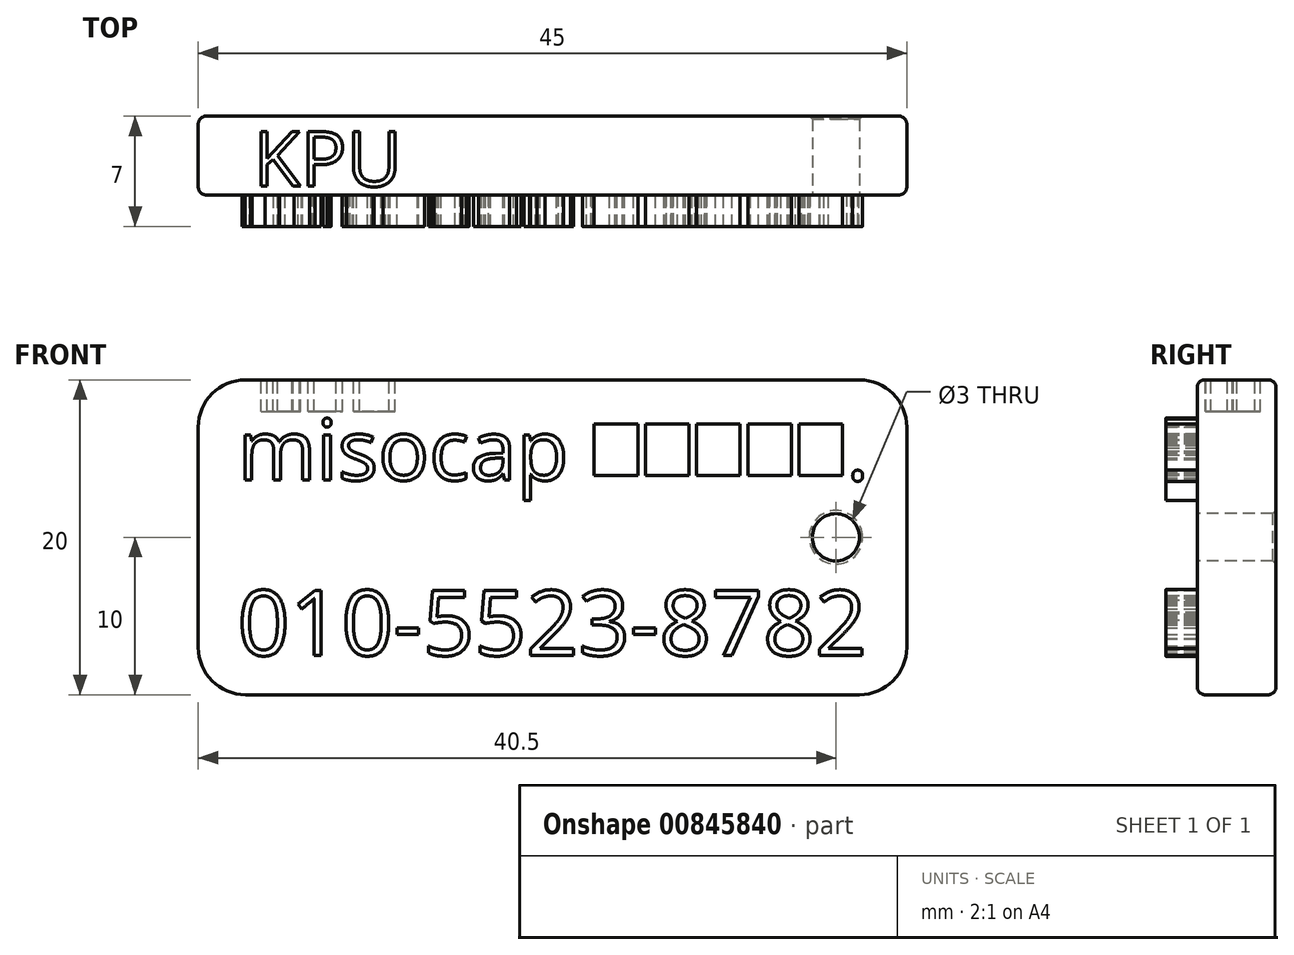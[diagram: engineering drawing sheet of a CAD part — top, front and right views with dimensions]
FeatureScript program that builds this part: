
annotation { "Feature Type Name" : "Feature", "Feature Type Description" : "" }
export const myFeature = defineFeature(function(context is Context, id is Id, definition is map)
    precondition{}
    {
        {
            var Q0;
            Q0=qCreatedBy(makeId("Front.planeOp"),FACE);
            var sketch = newSketch(context, id + "F0", { "sketchPlane" : qUnion([Q0])});
            skLineSegment(sketch, "E0.bottom", {"start": v(22.5, 10) * mm, "end": v(-22.5, 10) * mm});
            skLineSegment(sketch, "E0.top", {"start": v(22.5, -10) * mm, "end": v(-22.5, -10) * mm});
            skLineSegment(sketch, "E0.left", {"start": v(22.5, 10) * mm, "end": v(22.5, -10) * mm});
            skLineSegment(sketch, "E0.right", {"start": v(-22.5, 10) * mm, "end": v(-22.5, -10) * mm});
            skPoint(sketch, "E0.middle", {"position": v(0, 0) * mm});
            skSolve(sketch);
        }
        {
            var Q0;
            Q0 = qSketchRegion(id + "F0", true);
            extrude(context, id + "F1", {"entities" : qUnion([Q0]), "depth" : 5 * mm, "offsetDistance" : 25 * mm});
        }
        {
            var Q0;
            Q0=makeQuery(id+"F1.opExtrude","CAP_FACE",FACE,{"disambiguationData":[OSD([sQuery(id+"F0.wireOp",EDGE,"E0.bottom"),sQuery(id+"F0.wireOp",EDGE,"E0.top"),sQuery(id+"F0.wireOp",EDGE,"E0.left"),sQuery(id+"F0.wireOp",EDGE,"E0.right")])],"isStart":false});
            var sketch = newSketch(context, id + "F2", { "sketchPlane" : qUnion([Q0])});
            skText(sketch, "E1", { "text": "misocap 반갑습니다.", "fontName": "OpenSans-Regular.ttf"});
            const initialGuessF2  = {"E1": [-0.02, 0.00363, 1, 0, 0.00387]};
            skSetInitialGuess(sketch, initialGuessF2);
            skSolve(sketch);
        }
        {
            var Q0;
            Q0 = qSketchRegion(id + "F2", true);
            extrude(context, id + "F3", {"entities" : qUnion([Q0]), "operationType" : NewBodyOperationType.ADD, "depth" : 2 * mm, "offsetDistance" : 25 * mm});
        }
        {
            var Q0;
            {var subQ0=sQuery(id+"F0.wireOp",EDGE,"E0.top");var subQ1=sQuery(id+"F0.wireOp",EDGE,"E0.right");var subQ2=sQuery(id+"F0.wireOp",EDGE,"E0.bottom");var subQ3=sQuery(id+"F0.wireOp",EDGE,"E0.left");Q0=makeQuery(id+"F3.boolean.opBoolean","SPLIT",FACE,{"disambiguationData":[TD([makeQuery(id+"F1.opExtrude","SWEPT_FACE",FACE,{"disambiguationData":[OSD([subQ2])]})])],"derivedFrom":makeQuery(id+"F1.opExtrude","CAP_FACE",FACE,{"disambiguationData":[OSD([subQ2,subQ0,subQ3,subQ1])],"isStart":false})});}
            var sketch = newSketch(context, id + "F4", { "sketchPlane" : qUnion([Q0])});
            skText(sketch, "E2", { "text": "010-5523-8782", "fontName": "OpenSans-Regular.ttf"});
            const initialGuessF4  = {"E2": [-0.02, -0.0075, 1, 0, 0.00415]};
            skSetInitialGuess(sketch, initialGuessF4);
            skSolve(sketch);
        }
        {
            var Q0;
            Q0 = qSketchRegion(id + "F4", true);
            extrude(context, id + "F5", {"entities" : qUnion([Q0]), "operationType" : NewBodyOperationType.ADD, "depth" : 2 * mm, "offsetDistance" : 25 * mm});
        }
        {
            var Q0;
            Q0=makeQuery(id+"F1.opExtrude","SWEPT_EDGE",EDGE,{"disambiguationData":[OSD([sQuery(id+"F0.wireOp",EDGE,"E0.bottom"),sQuery(id+"F0.wireOp",EDGE,"E0.right")])]});
            var Q1;
            Q1=makeQuery(id+"F1.opExtrude","SWEPT_EDGE",EDGE,{"disambiguationData":[OSD([sQuery(id+"F0.wireOp",EDGE,"E0.top"),sQuery(id+"F0.wireOp",EDGE,"E0.right")])]});
            var Q2;
            Q2=makeQuery(id+"F1.opExtrude","SWEPT_EDGE",EDGE,{"disambiguationData":[OSD([sQuery(id+"F0.wireOp",EDGE,"E0.top"),sQuery(id+"F0.wireOp",EDGE,"E0.left")])]});
            var Q3;
            Q3=makeQuery(id+"F1.opExtrude","SWEPT_EDGE",EDGE,{"disambiguationData":[OSD([sQuery(id+"F0.wireOp",EDGE,"E0.bottom"),sQuery(id+"F0.wireOp",EDGE,"E0.left")])]});
            fillet(context, id + "F6", {"entities" : qUnion([Q0, Q1, Q2, Q3]), "radius" : 3 * mm, "tangentPropagation" : true, "allowEdgeOverflow" : false});
        }
        {
            var Q0;
            Q0=makeQuery(id+"F1.opExtrude","SWEPT_FACE",FACE,{"disambiguationData":[OSD([sQuery(id+"F0.wireOp",EDGE,"E0.bottom")])]});
            var sketch = newSketch(context, id + "F7", { "sketchPlane" : qUnion([Q0])});
            skText(sketch, "E3", { "text": "KPU", "fontName": "OpenSans-Regular.ttf"});
            const initialGuessF7  = {"E3": [-0.019, -0.00445, 1, 0, 0.0035]};
            skSetInitialGuess(sketch, initialGuessF7);
            skSolve(sketch);
        }
        {
            var Q0;
            Q0 = qSketchRegion(id + "F7", true);
            extrude(context, id + "F8", {"entities" : qUnion([Q0]), "operationType" : NewBodyOperationType.REMOVE, "oppositeDirection" : true, "depth" : 2 * mm, "offsetDistance" : 25 * mm});
        }
        {
            var Q0;
            Q0=makeQuery(id+"F4.imprint","IMPRINT",FACE,{"disambiguationData":[TD([[makeQuery(id+"F4.imprint","IMPRINT",EDGE,{"derivedFrom":sQuery(id+"F4.wireOp",EDGE,"E2.sketch_text.stroke-0")}),1.0]])]});
            var sketch = newSketch(context, id + "F9", { "sketchPlane" : qUnion([Q0])});
            skCircle(sketch, "E4", {"center": v(18, 0) * mm, "radius": 1.5 * mm});
            skSolve(sketch);
        }
        {
            var Q0;
            Q0 = qSketchRegion(id + "F9", true);
            extrude(context, id + "F10", {"entities" : qUnion([Q0]), "operationType" : NewBodyOperationType.REMOVE, "oppositeDirection" : true, "depth" : 25 * mm, "offsetDistance" : 25 * mm});
        }
        {
            var Q0;
            Q0=makeQuery(id+"F10.boolean.opBoolean","COPY",EDGE,{"derivedFrom":makeQuery(id+"F10.opExtrude","CAP_EDGE",EDGE,{"disambiguationData":[OSD([sQuery(id+"F9.wireOp",EDGE,"E4")])],"isStart":true})});
            var Q1;
            Q1=makeQuery(id+"F10.boolean.opBoolean","INTERSECT",EDGE,{"derivedFrom":[makeQuery(id+"F1.opExtrude","CAP_FACE",FACE,{"disambiguationData":[OSD([sQuery(id+"F0.wireOp",EDGE,"E0.bottom"),sQuery(id+"F0.wireOp",EDGE,"E0.top"),sQuery(id+"F0.wireOp",EDGE,"E0.left"),sQuery(id+"F0.wireOp",EDGE,"E0.right")])],"isStart":true}),makeQuery(id+"F10.opExtrude","SWEPT_FACE",FACE,{"disambiguationData":[OSD([sQuery(id+"F9.wireOp",EDGE,"E4")])]})]});
            chamfer(context, id + "F11", {"entities" : qUnion([Q0, Q1]), "width" : 0.2 * mm, "tangentPropagation" : true});
        }
        {
            var Q0;
            Q0=makeQuery(id+"F1.opExtrude","CAP_EDGE",EDGE,{"disambiguationData":[OSD([sQuery(id+"F0.wireOp",EDGE,"E0.bottom")])],"isStart":false});
            var Q1;
            Q1=makeQuery(id+"F1.opExtrude","CAP_EDGE",EDGE,{"disambiguationData":[OSD([sQuery(id+"F0.wireOp",EDGE,"E0.bottom")])],"isStart":true});
            fillet(context, id + "F12", {"entities" : qUnion([Q0, Q1]), "radius" : 0.5 * mm, "tangentPropagation" : true, "allowEdgeOverflow" : false});
        }
    });
